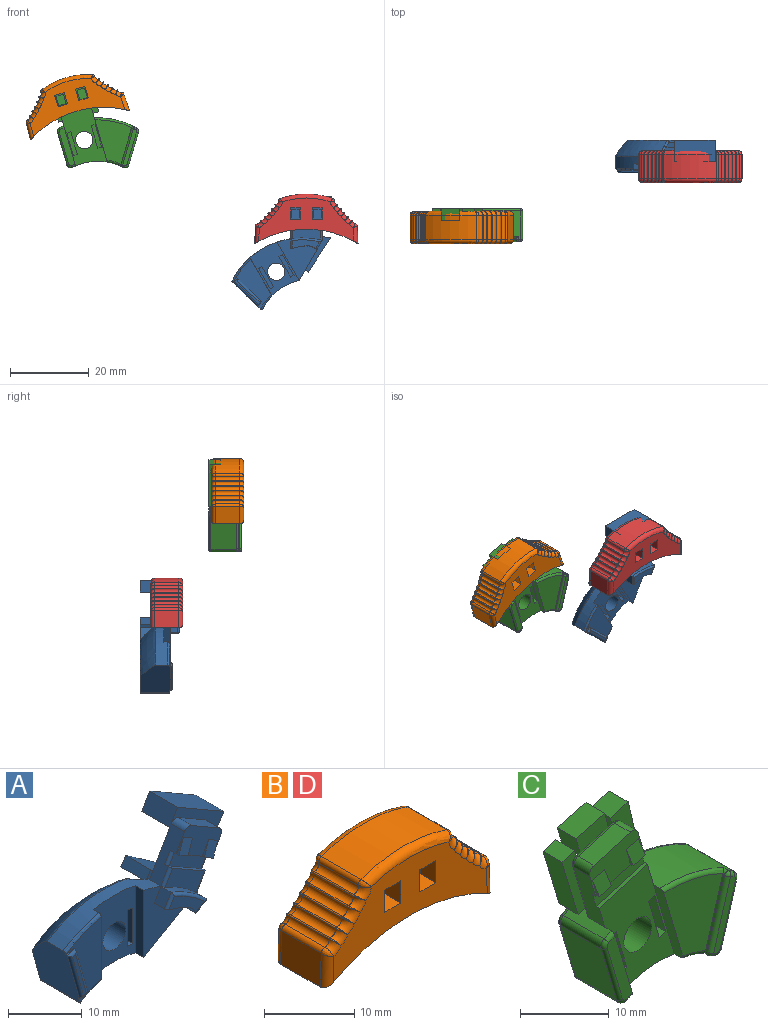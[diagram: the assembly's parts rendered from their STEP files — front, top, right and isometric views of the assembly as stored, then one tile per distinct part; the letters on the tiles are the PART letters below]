
ASSEMBLY  parts=4 mates=2
PART A: 93 faces, bbox 34.7x10.1x21.5 mm
  f0: plane 2.17x1.95mm, normal (-0.87,0,0.5), area 4.9mm2, adj f17,f19,f24,f74
  f1: plane 11.58x8mm, normal (0,-1,0), area 61.3mm2, adj f18,f23,f25,f27,f29,f40,f41,f42
  f2: plane 9.37x8mm, normal (-0.87,0,0.5), area 34.2mm2, adj f3,f8,f9,f15,f18,f53,f75,f77
  f3: plane 8.71x7.36mm, normal (0,-1,0), area 24mm2, adj f2,f4,f5,f6,f9,f10,f11,f12
  f4: plane 7.58x4.38mm, normal (0.87,0,-0.5), area 18.8mm2, adj f3,f8,f9,f15,f20,f52,f76,f78
  f5: plane 3.17x2.98mm, normal (0.08,-0.99,0.14), area 5.1mm2, adj f3,f9,f12,f14
  f6: plane 5.2x3mm, normal (0.5,0,0.87), area 15.6mm2, adj f3,f52,f53,f84
  f7: plane 7.58x6.36mm, normal (0,-1,0), area 20.1mm2, adj f15,f17,f75,f78
  f8: plane 11.14x10.83mm, normal (0,1,0), area 62mm2, adj f2,f4,f18,f81
  f9: plane 6.93x4mm, normal (-0.5,0,-0.87), area 7.3mm2, adj f2,f3,f4,f5,f10,f11,f12,f13
  f10: plane 3.17x2.98mm, normal (0.08,-0.99,0.14), area 5.1mm2, adj f3,f9,f11,f13
  f11: plane 2.17x1.25mm, normal (0.87,0,-0.5), area 0.5mm2, adj f3,f9,f10
  f12: plane 2.17x1.25mm, normal (-0.87,0,0.5), area 0.5mm2, adj f3,f5,f9
  f13: plane 2.17x1.25mm, normal (-0.87,0,0.5), area 0.5mm2, adj f3,f9,f10
  f14: plane 2.17x1.25mm, normal (0.87,0,-0.5), area 0.5mm2, adj f3,f5,f9
  f15: plane 6.93x4mm, normal (0.5,0,0.87), area 5.6mm2, adj f2,f4,f7,f16,f75,f76,f77,f78
  f16: plane 7.2x5.37mm, normal (0,-1,0), area 14.9mm2, adj f9,f15,f76,f77
  f17: cylinder r=20mm len=6.71mm, axis (0,1,0), area 12.6mm2, adj f0,f7,f18,f20,f73,f75,f78
  f18: cylinder r=20mm len=25mm, axis (0,1,0), area 50.2mm2, adj f1,f2,f8,f17,f20,f23,f24,f29
  f19: extruded ~5.8x3.46mm, area 16.6mm2, adj f0,f20,f21,f24,f72,f74
  f20: plane 10.06x6.52mm, normal (0.5,0,-0.87), area 34.4mm2, adj f4,f17,f18,f19,f23,f24,f25,f54
  f21: plane 6.88x4.81mm, normal (0,-1,0), area 10.9mm2, adj f19,f72,f73,f74
  f22: plane 6.93x5.53mm, normal (0,1,0), area 19.2mm2, adj f38,f56,f85,f89,f90
  f23: plane 11.18x1.6mm, normal (-1,0,0), area 17.9mm2, adj f1,f18,f20,f24
  f24: plane 11.18x7.89mm, normal (0,-1,0), area 46.3mm2, adj f0,f18,f19,f20,f23
  f25: cylinder r=14mm len=11.54mm, axis (0,1,0), area 70.7mm2, adj f1,f20,f26,f29,f54,f58,f60,f62
  f26: plane 8.89x1.46mm, normal (1,0,0), area 10.7mm2, adj f25,f38,f54,f63,f65,f66
  f27: cylinder r=2.2mm len=6mm, axis (0,1,0), area 82.9mm2, adj f1,f28
  f28: plane 13.39x9.12mm, normal (0,1,0), area 62.6mm2, adj f27,f30,f36,f39,f60,f62,f63,f66
  f29: plane 11.23x1.55mm, normal (1,0,0), area 16.7mm2, adj f1,f18,f25,f31,f58,f71
  f30: plane 9.75x7.81mm, normal (-0.96,0,-0.27), area 70.5mm2, adj f18,f28,f31,f32,f34,f39,f60,f70
  f31: plane 12.21x6.81mm, normal (0,-1,0), area 45.5mm2, adj f29,f30,f32,f33,f34,f58,f60,f71
  f32: plane 1.44x0.41mm, normal (0.27,0,-0.96), area 0.4mm2, adj f30,f31,f33,f68
  f33: plane 8.18x2.3mm, normal (0.96,0,0.27), area 2.1mm2, adj f31,f32,f34,f67
  f34: plane 1.44x0.41mm, normal (-0.27,0,0.96), area 0.4mm2, adj f30,f31,f33,f69
  f35: plane 7.48x2.63mm, normal (0,-1,0), area 4.6mm2, adj f67,f68,f69,f70
  f36: cylinder r=1.3mm len=5.4mm, axis (0,1,0), area 44.1mm2, adj f28,f37
  f37: plane 2.6x2.6mm, normal (0,1,0), area 5.3mm2, adj f36
  f38: cylinder r=3mm len=10.38mm, axis (0,0,-1), area 42.8mm2, adj f22,f26,f54,f57,f61,f64,f85,f86
  f39: bspline ~18.82x8.23mm, area 85.4mm2, adj f18,f28,f30,f59,f61,f64,f65
  f40: plane 6x3mm, normal (-1,0,0), area 18mm2, adj f1,f41,f44,f45
  f41: plane 3x0.42mm, normal (0,0,-1), area 1.3mm2, adj f1,f40,f42,f45
  f42: cylinder r=21.4mm len=3mm, axis (0,1,0), area 1.8mm2, adj f1,f41,f43,f45
  f43: plane 5.91x3mm, normal (1,0,0), area 17.7mm2, adj f1,f42,f44,f45
  f44: plane 3x1mm, normal (0,0,1), area 3mm2, adj f1,f40,f43,f45
  f45: plane 6x1mm, normal (0,-1,0), area 6mm2, adj f40,f41,f42,f43,f44
  f46: plane 3x0.42mm, normal (0,0,-1), area 1.3mm2, adj f1,f47,f50,f51
  f47: plane 6x3mm, normal (1,0,0), area 18mm2, adj f1,f46,f48,f51
  f48: plane 3x1mm, normal (0,0,1), area 3mm2, adj f1,f47,f49,f51
  f49: plane 5.91x3mm, normal (-1,0,0), area 17.7mm2, adj f1,f48,f50,f51
  f50: cylinder r=21.4mm len=3mm, axis (0,1,0), area 1.8mm2, adj f1,f46,f49,f51
  f51: plane 6x1mm, normal (0,-1,0), area 6mm2, adj f46,f47,f48,f49,f50
  f52: cylinder r=1mm len=2.6mm, axis (0,1,0), area 4.1mm2, adj f3,f4,f6,f84
  f53: cylinder r=1mm len=2.6mm, axis (0,1,0), area 4.1mm2, adj f2,f3,f6,f84
  f54: bspline ~4.68x3.45mm, area 3mm2, adj f20,f25,f26,f38,f55,f86,f87
  f55: cylinder r=0.45mm len=7.06mm, axis (0.87,0,0.5), area 5.4mm2, adj f20,f54,f56,f87
  f56: torus R=19.55mm, axis (0,-1,0), area 5.6mm2, adj f18,f22,f55,f57,f87
  f57: bspline ~3.69x1.67mm, area 1.9mm2, adj f18,f38,f56,f59
  f58: torus R=14.45mm, axis (0,-1,0), area 3mm2, adj f25,f29,f31,f60
  f59: bspline ~0.44x0.28mm, area 0mm2, adj f39,f57,f61
  f60: cylinder r=0.45mm len=7.5mm, axis (0,1,0), area 6.1mm2, adj f25,f28,f30,f31,f58,f62
  f61: bspline ~2.6x2.46mm, area 1.6mm2, adj f38,f39,f59,f64
  f62: torus R=14.45mm, axis (0,-1,0), area 8.5mm2, adj f25,f28,f60,f63
  f63: cylinder r=0.45mm len=7.03mm, axis (0,0,1), area 4.8mm2, adj f26,f28,f62,f66
  f64: bspline ~0.42x0.4mm, area 0.1mm2, adj f38,f39,f61,f65
  f65: bspline ~1.97x1.8mm, area 1.5mm2, adj f26,f39,f64,f66
  f66: bspline ~0.45x0.45mm, area 0.1mm2, adj f26,f28,f63,f65
  f67: cylinder r=0.45mm len=8.31mm, axis (0.27,0,-0.96), area 5.7mm2, adj f33,f35,f68,f69
  f68: cylinder r=0.45mm len=1.57mm, axis (-0.96,0,-0.27), area 0.7mm2, adj f32,f35,f67,f70
  f69: cylinder r=0.45mm len=1.57mm, axis (0.96,0,0.27), area 0.7mm2, adj f34,f35,f67,f70
  f70: cylinder r=0.45mm len=8.31mm, axis (-0.27,0,0.96), area 5.7mm2, adj f30,f35,f68,f69
  f71: torus R=19.55mm, axis (0,-1,0), area 5.3mm2, adj f18,f29,f30,f31
  f72: cylinder r=0.45mm len=2.46mm, axis (-0.87,0,-0.5), area 1.6mm2, adj f19,f20,f21,f73
  f73: torus R=19.55mm, axis (0,-1,0), area 5.3mm2, adj f17,f21,f72,f74
  f74: cylinder r=0.45mm len=2.39mm, axis (0.5,0,0.87), area 1.6mm2, adj f0,f19,f21,f73
  f75: cylinder r=0.45mm len=2.75mm, axis (0.5,0,0.87), area 2mm2, adj f2,f7,f15,f17
  f76: cylinder r=0.45mm len=2.04mm, axis (-0.5,0,-0.87), area 1.5mm2, adj f4,f9,f15,f16
  f77: cylinder r=0.45mm len=2.04mm, axis (0.5,0,0.87), area 1.5mm2, adj f2,f9,f15,f16
  f78: cylinder r=0.45mm len=3.13mm, axis (-0.5,0,-0.87), area 2.3mm2, adj f4,f7,f15,f17
  f79: plane 10.4x7.74mm, normal (0,1,0), area 30.8mm2, adj f2,f80,f81,f82,f83
  f80: plane 5.4x1.86mm, normal (-0.52,0,-0.85), area 11.8mm2, adj f79,f81,f83,f84
  f81: plane 6.93x5.4mm, normal (-0.5,0,-0.87), area 43.2mm2, adj f2,f8,f79,f80
  f82: plane 8.9x5.4mm, normal (0.5,0,0.87), area 55.5mm2, adj f2,f79,f83,f84
  f83: plane 5.4x2.6mm, normal (0.85,0,-0.53), area 16.5mm2, adj f79,f80,f82,f84
  f84: plane 10.15x7.74mm, normal (0,-1,0), area 19.2mm2, adj f2,f4,f6,f52,f53,f80,f82,f83
  f85: plane 5.84x4.8mm, normal (-0.48,0,0.88), area 32mm2, adj f22,f38,f86,f88,f89
  f86: plane 4.8x2.15mm, normal (-0.99,0,-0.13), area 10.4mm2, adj f38,f54,f85,f87,f88,f92
  f87: plane 10.51x9.6mm, normal (0,-1,0), area 26.2mm2, adj f54,f55,f56,f86,f90,f91,f92
  f88: plane 10.51x9.7mm, normal (0,1,0), area 33mm2, adj f85,f86,f89,f90,f91,f92
  f89: plane 5.3x4.8mm, normal (-0.57,0,-0.82), area 31.1mm2, adj f22,f85,f88,f90
  f90: plane 4.8x1.42mm, normal (-0.82,0,0.57), area 8.3mm2, adj f22,f87,f88,f89,f91
  f91: plane 8.16x5.73mm, normal (0.57,0,0.82), area 47.9mm2, adj f87,f88,f90,f92
  f92: plane 9.4x4.8mm, normal (0.45,0,-0.89), area 50.6mm2, adj f86,f87,f88,f91
PART B: 107 faces, bbox 26.2x8.2x14.3 mm
  f0: plane 8.3x1.05mm, normal (0,1,0), area 6.8mm2, adj f1,f5,f21,f33
  f1: plane 7.2x3.3mm, normal (-1,0,0), area 23.2mm2, adj f0,f3,f5,f22,f23,f32,f33,f34
  f2: plane 24.15x11.01mm, normal (0,-1,0), area 137mm2, adj f5,f24,f25,f26,f27,f28,f29,f30
  f3: plane 8.3x4.75mm, normal (0,1,0), area 24.5mm2, adj f1,f21,f22,f24,f25,f26,f27,f28
  f4: plane 6.2x4.47mm, normal (-1,0,0.04), area 27.7mm2, adj f5,f48,f49,f78
  f5: cylinder r=25mm len=26.2mm, axis (0,1,0), area 197.6mm2, adj f0,f1,f2,f4,f6,f20,f21,f23
  f6: plane 6.2x4.47mm, normal (1,0,0.04), area 27.7mm2, adj f5,f45,f77,f106
  f7: cylinder r=0.68mm len=6.2mm, axis (0,1,0), area 7.3mm2, adj f35,f45,f75,f104
  f8: cylinder r=0.68mm len=6.2mm, axis (0,1,0), area 9.1mm2, adj f35,f36,f73,f102
  f9: cylinder r=0.68mm len=6.2mm, axis (0,1,0), area 9.1mm2, adj f36,f37,f71,f100
  f10: cylinder r=0.68mm len=6.2mm, axis (0,1,0), area 9.1mm2, adj f37,f38,f69,f98
  f11: cylinder r=0.68mm len=6.2mm, axis (0,1,0), area 9.1mm2, adj f38,f39,f67,f96
  f12: cylinder r=0.68mm len=6.2mm, axis (0,1,0), area 7.9mm2, adj f39,f46,f65,f94
  f13: cylinder r=20mm len=13.45mm, axis (0,1,0), area 85mm2, adj f46,f47,f63,f92
  f14: cylinder r=0.68mm len=6.2mm, axis (0,1,0), area 7.9mm2, adj f40,f47,f61,f90
  f15: cylinder r=0.68mm len=6.2mm, axis (0,1,0), area 9.1mm2, adj f40,f41,f59,f88
  f16: cylinder r=0.68mm len=6.2mm, axis (0,1,0), area 9.1mm2, adj f41,f42,f57,f86
  f17: cylinder r=0.68mm len=6.2mm, axis (0,1,0), area 9.1mm2, adj f42,f43,f55,f84
  f18: cylinder r=0.68mm len=6.2mm, axis (0,1,0), area 9.1mm2, adj f43,f44,f53,f82
  f19: cylinder r=0.68mm len=6.2mm, axis (0,1,0), area 7.3mm2, adj f44,f48,f51,f80
  f20: plane 24.15x11.01mm, normal (0,1,0), area 152mm2, adj f5,f78,f80,f82,f84,f86,f88,f90
  f21: plane 7.2x3.3mm, normal (1,0,0), area 23.2mm2, adj f0,f3,f5,f22,f23,f32,f33,f34
  f22: plane 8.3x3.3mm, normal (0,0,-1), area 27.4mm2, adj f1,f3,f21,f23
  f23: plane 8.3x7.2mm, normal (0,-1,0), area 57.8mm2, adj f1,f5,f21,f22
  f24: plane 3x2.45mm, normal (1,0,0), area 7.4mm2, adj f2,f3,f25,f26
  f25: plane 2.5x2.45mm, normal (0,0,1), area 6.1mm2, adj f2,f3,f24,f27
  f26: plane 2.5x2.45mm, normal (0,0,-1), area 6.1mm2, adj f2,f3,f24,f27
  f27: plane 3x2.45mm, normal (-1,0,0), area 7.4mm2, adj f2,f3,f25,f26
  f28: plane 3x2.45mm, normal (1,0,0), area 7.4mm2, adj f2,f3,f29,f30
  f29: plane 2.5x2.45mm, normal (0,0,1), area 6.1mm2, adj f2,f3,f28,f31
  f30: plane 2.5x2.45mm, normal (0,0,-1), area 6.1mm2, adj f2,f3,f28,f31
  f31: plane 3x2.45mm, normal (-1,0,0), area 7.4mm2, adj f2,f3,f29,f30
  f32: plane 8.3x0.4mm, normal (0,0,1), area 3.3mm2, adj f1,f3,f21,f34
  f33: plane 8.3x0.4mm, normal (0,0,-1), area 3.3mm2, adj f0,f1,f21,f34
  f34: plane 8.3x1.4mm, normal (0,1,0), area 11.6mm2, adj f1,f21,f32,f33
  f35: cylinder r=0.1mm len=6.2mm, axis (0,1,0), area 1.3mm2, adj f7,f8,f74,f103
  f36: cylinder r=0.1mm len=6.2mm, axis (0,1,0), area 1.3mm2, adj f8,f9,f72,f101
  f37: cylinder r=0.1mm len=6.2mm, axis (0,1,0), area 1.3mm2, adj f9,f10,f70,f99
  f38: cylinder r=0.1mm len=6.2mm, axis (0,1,0), area 1.3mm2, adj f10,f11,f68,f97
  f39: cylinder r=0.1mm len=6.2mm, axis (0,1,0), area 1.3mm2, adj f11,f12,f66,f95
  f40: cylinder r=0.1mm len=6.2mm, axis (0,1,0), area 1.3mm2, adj f14,f15,f60,f89
  f41: cylinder r=0.1mm len=6.2mm, axis (0,1,0), area 1.3mm2, adj f15,f16,f58,f87
  f42: cylinder r=0.1mm len=6.2mm, axis (0,1,0), area 1.3mm2, adj f16,f17,f56,f85
  f43: cylinder r=0.1mm len=6.2mm, axis (0,1,0), area 1.3mm2, adj f17,f18,f54,f83
  f44: cylinder r=0.1mm len=6.2mm, axis (0,1,0), area 1.3mm2, adj f18,f19,f52,f81
  f45: cylinder r=0.6mm len=6.2mm, axis (0,1,0), area 5.6mm2, adj f6,f7,f76,f105
  f46: cylinder r=0.6mm len=6.2mm, axis (0,-1,0), area 5.3mm2, adj f12,f13,f64,f93
  f47: cylinder r=0.6mm len=6.2mm, axis (0,-1,0), area 5.3mm2, adj f13,f14,f62,f91
  f48: cylinder r=0.6mm len=6.2mm, axis (0,1,0), area 5.6mm2, adj f4,f19,f50,f79
  f49: cylinder r=1mm len=4.51mm, axis (0.04,0,1), area 6.5mm2, adj f2,f4,f5,f50
  f50: bspline ~1x0.99mm, area 0.9mm2, adj f48,f49,f51
  f51: torus R=1.68mm, axis (0,-1,0), area 2mm2, adj f2,f19,f50,f52
  f52: bspline ~1.04x1.03mm, area 0.1mm2, adj f44,f51,f53
  f53: torus R=1.68mm, axis (0,-1,0), area 2.3mm2, adj f2,f18,f52,f54
  f54: bspline ~1.04x0.98mm, area 0.1mm2, adj f43,f53,f55
  f55: torus R=1.68mm, axis (0,-1,0), area 2.3mm2, adj f2,f17,f54,f56
  f56: bspline ~1.04x0.99mm, area 0.1mm2, adj f42,f55,f57
  f57: torus R=1.68mm, axis (0,-1,0), area 2.3mm2, adj f2,f16,f56,f58
  f58: bspline ~1.04x1.04mm, area 0.1mm2, adj f41,f57,f59
  f59: torus R=1.68mm, axis (0,-1,0), area 2.3mm2, adj f2,f15,f58,f60
  f60: bspline ~1.08x1.04mm, area 0.1mm2, adj f40,f59,f61
  f61: torus R=1.68mm, axis (0,-1,0), area 2.3mm2, adj f2,f14,f60,f62
  f62: bspline ~1.26x1.11mm, area 0.8mm2, adj f47,f61,f63
  f63: torus R=19mm, axis (0,-1,0), area 20.8mm2, adj f2,f13,f62,f64
  f64: bspline ~1.26x1.11mm, area 0.8mm2, adj f46,f63,f65
  f65: torus R=1.68mm, axis (0,-1,0), area 2.3mm2, adj f2,f12,f64,f66
  f66: bspline ~1.08x1.04mm, area 0.1mm2, adj f39,f65,f67
  f67: torus R=1.68mm, axis (0,-1,0), area 2.3mm2, adj f2,f11,f66,f68
  f68: bspline ~1.04x1.04mm, area 0.1mm2, adj f38,f67,f69
  f69: torus R=1.68mm, axis (0,-1,0), area 2.3mm2, adj f2,f10,f68,f70
  f70: bspline ~1.04x0.99mm, area 0.1mm2, adj f37,f69,f71
  f71: torus R=1.68mm, axis (0,-1,0), area 2.3mm2, adj f2,f9,f70,f72
  f72: bspline ~1.04x0.98mm, area 0.1mm2, adj f36,f71,f73
  f73: torus R=1.68mm, axis (0,-1,0), area 2.3mm2, adj f2,f8,f72,f74
  f74: bspline ~1.04x1.03mm, area 0.1mm2, adj f35,f73,f75
  f75: torus R=1.68mm, axis (0,-1,0), area 2mm2, adj f2,f7,f74,f76
  f76: bspline ~1.27x0.99mm, area 0.9mm2, adj f45,f75,f77
  f77: cylinder r=1mm len=4.51mm, axis (0.04,0,-1), area 6.5mm2, adj f2,f5,f6,f76
  f78: cylinder r=1mm len=4.51mm, axis (-0.04,0,-1), area 6.5mm2, adj f4,f5,f20,f79
  f79: bspline ~1.27x0.99mm, area 0.9mm2, adj f48,f78,f80
  f80: torus R=1.68mm, axis (0,-1,0), area 2mm2, adj f19,f20,f79,f81
  f81: bspline ~1.16x1.03mm, area 0.1mm2, adj f44,f80,f82
  f82: torus R=1.68mm, axis (0,-1,0), area 2.3mm2, adj f18,f20,f81,f83
  f83: bspline ~1.16x0.98mm, area 0.1mm2, adj f43,f82,f84
  f84: torus R=1.68mm, axis (0,-1,0), area 2.3mm2, adj f17,f20,f83,f85
  f85: bspline ~1.16x0.99mm, area 0.1mm2, adj f42,f84,f86
  f86: torus R=1.68mm, axis (0,-1,0), area 2.3mm2, adj f16,f20,f85,f87
  f87: bspline ~1.16x1.04mm, area 0.1mm2, adj f41,f86,f88
  f88: torus R=1.68mm, axis (0,-1,0), area 2.3mm2, adj f15,f20,f87,f89
  f89: bspline ~1.16x1.08mm, area 0.1mm2, adj f40,f88,f90
  f90: torus R=1.68mm, axis (0,-1,0), area 2.3mm2, adj f14,f20,f89,f91
  f91: bspline ~1.26x1.11mm, area 0.8mm2, adj f47,f90,f92
  f92: torus R=19mm, axis (0,-1,0), area 20.8mm2, adj f13,f20,f91,f93
  f93: bspline ~1.26x1.11mm, area 0.8mm2, adj f46,f92,f94
  f94: torus R=1.68mm, axis (0,-1,0), area 2.3mm2, adj f12,f20,f93,f95
  f95: bspline ~1.16x1.08mm, area 0.1mm2, adj f39,f94,f96
  f96: torus R=1.68mm, axis (0,-1,0), area 2.3mm2, adj f11,f20,f95,f97
  f97: bspline ~1.16x1.04mm, area 0.1mm2, adj f38,f96,f98
  f98: torus R=1.68mm, axis (0,-1,0), area 2.3mm2, adj f10,f20,f97,f99
  f99: bspline ~1.16x0.99mm, area 0.1mm2, adj f37,f98,f100
  f100: torus R=1.68mm, axis (0,-1,0), area 2.3mm2, adj f9,f20,f99,f101
  f101: bspline ~1.16x0.98mm, area 0.1mm2, adj f36,f100,f102
  f102: torus R=1.68mm, axis (0,-1,0), area 2.3mm2, adj f8,f20,f101,f103
  f103: bspline ~1.16x1.03mm, area 0.1mm2, adj f35,f102,f104
  f104: torus R=1.68mm, axis (0,-1,0), area 2mm2, adj f7,f20,f103,f105
  f105: bspline ~1x0.99mm, area 0.9mm2, adj f45,f104,f106
  f106: cylinder r=1mm len=4.51mm, axis (-0.04,0,1), area 6.5mm2, adj f5,f6,f20,f105
PART C: 93 faces, bbox 23.2x8.4x23.5 mm
  f0: plane 10.38x8.77mm, normal (0,1,0), area 52.5mm2, adj f7,f53,f55,f57,f78,f79,f83,f84
  f1: plane 2.96x2.62mm, normal (-0.04,-0.99,0.15), area 5.1mm2, adj f2,f3,f36,f38
  f2: plane 1.92x0.57mm, normal (0.28,0.02,-0.96), area 0.8mm2, adj f1,f31,f36,f38
  f3: plane 8.65x6.14mm, normal (0,-1,0), area 24mm2, adj f1,f4,f5,f19,f31,f33,f35,f36
  f4: plane 8.43x2.5mm, normal (0.96,0,0.28), area 21mm2, adj f3,f6,f7,f30,f31,f32,f39,f53
  f5: plane 8.14x2.5mm, normal (-0.96,0,-0.28), area 20.2mm2, adj f3,f6,f7,f30,f31,f32,f40,f57
  f6: plane 15.53x11.94mm, normal (0,-1,0), area 84.8mm2, adj f4,f5,f8,f13,f15,f16,f20,f21
  f7: cylinder r=20mm len=19.62mm, axis (0,1,0), area 101.8mm2, adj f0,f4,f5,f13,f16,f41,f44,f52
  f8: cylinder r=14mm len=12.88mm, axis (0,1,0), area 79.1mm2, adj f6,f13,f16,f42,f43,f45,f62,f65
  f9: plane 8.24x7.3mm, normal (0.96,0,-0.28), area 62.7mm2, adj f43,f44,f48,f64
  f10: plane 9.23x2.72mm, normal (-0.96,0,0.28), area 2.9mm2, adj f14,f59,f62,f65,f66
  f11: plane 9.47x3.52mm, normal (0,-1,0), area 9.5mm2, adj f60,f61,f64,f66,f67,f69
  f12: plane 19.64x11.68mm, normal (0,1,0), area 159.8mm2, adj f15,f45,f46,f47,f48,f49,f50,f51
  f13: plane 11.23x3.34mm, normal (-0.96,0,-0.28), area 17.4mm2, adj f6,f7,f8,f14,f58,f62
  f14: plane 11.23x9.37mm, normal (0,-1,0), area 66.4mm2, adj f10,f13,f58,f59,f62
  f15: cylinder r=2.2mm len=6mm, axis (0,1,0), area 82.9mm2, adj f6,f12
  f16: plane 10.26x3.04mm, normal (0.96,0,0.28), area 15.9mm2, adj f6,f7,f8,f18,f70,f74
  f17: plane 8.24x6.5mm, normal (-0.96,0,-0.28), area 55.8mm2, adj f41,f42,f49,f72
  f18: plane 9.7x3.98mm, normal (0,-1,0), area 14.3mm2, adj f16,f70,f71,f72,f73,f74
  f19: plane 5.76x2.5mm, normal (-0.28,0,0.96), area 15mm2, adj f3,f39,f40,f55
  f20: plane 3x1.01mm, normal (-0.28,0,0.96), area 3.1mm2, adj f6,f21,f23,f24
  f21: plane 5.76x3mm, normal (-0.96,0,-0.28), area 18mm2, adj f6,f20,f22,f24
  f22: plane 3x1.01mm, normal (0.28,0,-0.96), area 3.2mm2, adj f6,f21,f23,f24
  f23: plane 5.76x3mm, normal (0.96,0,0.28), area 18mm2, adj f6,f20,f22,f24
  f24: plane 6.05x2.7mm, normal (0,-1,0), area 6.3mm2, adj f20,f21,f22,f23
  f25: plane 5.76x3mm, normal (0.96,0,0.28), area 18mm2, adj f6,f26,f28,f29
  f26: plane 3x1.01mm, normal (-0.28,0,0.96), area 3.1mm2, adj f6,f25,f27,f29
  f27: plane 5.76x3mm, normal (-0.96,0,-0.28), area 18mm2, adj f6,f26,f28,f29
  f28: plane 3x1.01mm, normal (0.28,0,-0.96), area 3.1mm2, adj f6,f25,f27,f29
  f29: plane 6.05x2.7mm, normal (0,-1,0), area 6.3mm2, adj f25,f26,f27,f28
  f30: plane 7.68x2.26mm, normal (-0.28,0,0.96), area 4mm2, adj f4,f5,f6,f32
  f31: plane 7.68x2.26mm, normal (0.28,0,-0.96), area 4mm2, adj f2,f3,f4,f5,f32,f34
  f32: plane 8.24x4.18mm, normal (0,-1,0), area 16mm2, adj f4,f5,f30,f31
  f33: plane 2.96x2.62mm, normal (-0.04,-0.99,0.15), area 5.1mm2, adj f3,f34,f35,f37
  f34: plane 1.92x0.57mm, normal (0.28,0.02,-0.96), area 0.8mm2, adj f31,f33,f35,f37
  f35: plane 2.4x0.71mm, normal (0.96,0,0.28), area 0.5mm2, adj f3,f33,f34
  f36: plane 2.4x0.71mm, normal (-0.96,0,-0.28), area 0.5mm2, adj f1,f2,f3
  f37: plane 2.4x0.71mm, normal (-0.96,0,-0.28), area 0.5mm2, adj f3,f33,f34
  f38: plane 2.4x0.71mm, normal (0.96,0,0.28), area 0.5mm2, adj f1,f2,f3
  f39: cylinder r=1mm len=2.5mm, axis (0,1,0), area 3.9mm2, adj f3,f4,f19,f54
  f40: cylinder r=1mm len=2.5mm, axis (0,1,0), area 3.9mm2, adj f3,f5,f19,f56
  f41: cylinder r=1mm len=6.5mm, axis (0,1,0), area 8.7mm2, adj f7,f17,f51,f71
  f42: cylinder r=1mm len=6.5mm, axis (0,1,0), area 11.5mm2, adj f8,f17,f47,f73
  f43: cylinder r=1mm len=7.3mm, axis (0,1,0), area 12.9mm2, adj f8,f9,f46,f67
  f44: cylinder r=1mm len=7.3mm, axis (0,1,0), area 9.8mm2, adj f7,f9,f50,f61
  f45: torus R=14.5mm, axis (0,-1,0), area 10.6mm2, adj f8,f12,f46,f47
  f46: torus R=0.5mm, axis (0,-1,0), area 1.1mm2, adj f12,f43,f45,f48
  f47: torus R=0.5mm, axis (0,-1,0), area 1.1mm2, adj f12,f42,f45,f49
  f48: cylinder r=0.5mm len=8.38mm, axis (0.28,0,0.96), area 6.7mm2, adj f9,f12,f46,f50
  f49: cylinder r=0.5mm len=8.38mm, axis (0.28,0,-0.96), area 6.7mm2, adj f12,f17,f47,f51
  f50: torus R=0.5mm, axis (0,-1,0), area 0.9mm2, adj f12,f44,f48,f52
  f51: torus R=0.5mm, axis (0,-1,0), area 0.9mm2, adj f12,f41,f49,f52
  f52: torus R=19.5mm, axis (0,-1,0), area 16mm2, adj f7,f12,f50,f51
  f53: cylinder r=0.5mm len=8.57mm, axis (-0.28,0,0.96), area 6.9mm2, adj f0,f4,f7,f54,f81
  f54: torus R=0.5mm, axis (0,-1,0), area 1mm2, adj f39,f53,f55,f81
  f55: cylinder r=0.5mm len=5.9mm, axis (-0.96,0,-0.28), area 4.7mm2, adj f0,f19,f54,f56,f75,f81,f87
  f56: torus R=0.5mm, axis (0,-1,0), area 1mm2, adj f40,f55,f57,f75
  f57: cylinder r=0.5mm len=8.28mm, axis (0.28,0,-0.96), area 6.6mm2, adj f0,f5,f7,f56,f75
  f58: torus R=19.5mm, axis (0,-1,0), area 8mm2, adj f7,f13,f14,f59
  f59: cylinder r=0.5mm len=0.8mm, axis (0,1,0), area 0.4mm2, adj f7,f10,f14,f58,f63
  f60: torus R=19.5mm, axis (0,-1,0), area 0.5mm2, adj f7,f11,f61,f63
  f61: torus R=0.5mm, axis (0,-1,0), area 0.9mm2, adj f11,f44,f60,f64
  f62: torus R=14.5mm, axis (0,-1,0), area 3mm2, adj f8,f10,f13,f14,f65
  f63: sphere r=0.5mm, area 0.5mm2, adj f59,f60,f66
  f64: cylinder r=0.5mm len=8.38mm, axis (-0.28,0,-0.96), area 6.7mm2, adj f9,f11,f61,f67
  f65: cylinder r=0.5mm len=0.8mm, axis (0,1,0), area 0.4mm2, adj f8,f10,f62,f68
  f66: cylinder r=0.5mm len=9.37mm, axis (0.28,0,0.96), area 7.6mm2, adj f10,f11,f63,f68
  f67: torus R=0.5mm, axis (0,-1,0), area 1.1mm2, adj f11,f43,f64,f69
  f68: sphere r=0.5mm, area 0.3mm2, adj f65,f66,f69
  f69: torus R=14.5mm, axis (0,-1,0), area 0.3mm2, adj f8,f11,f67,f68
  f70: torus R=19.5mm, axis (0,-1,0), area 0.9mm2, adj f7,f16,f18,f71
  f71: torus R=0.5mm, axis (0,-1,0), area 0.9mm2, adj f18,f41,f70,f72
  f72: cylinder r=0.5mm len=8.38mm, axis (-0.28,0,0.96), area 6.7mm2, adj f17,f18,f71,f73
  f73: torus R=0.5mm, axis (0,-1,0), area 1.1mm2, adj f18,f42,f72,f74
  f74: torus R=14.5mm, axis (0,-1,0), area 0.7mm2, adj f8,f16,f18,f73
  f75: plane 9.08x3.97mm, normal (0,-1,0), area 14mm2, adj f55,f56,f57,f77,f78,f79,f80
  f76: plane 9.08x4.3mm, normal (0,1,0), area 17.4mm2, adj f77,f78,f79,f80
  f77: plane 3x2.03mm, normal (-0.28,0,0.96), area 6.3mm2, adj f75,f76,f78,f80
  f78: plane 8.56x3mm, normal (0.97,0,0.26), area 26.6mm2, adj f0,f75,f76,f77,f79
  f79: plane 3x1.73mm, normal (0.29,0,-0.96), area 5.4mm2, adj f0,f75,f76,f78,f80
  f80: plane 8.5x3mm, normal (-0.96,0,-0.29), area 26.6mm2, adj f75,f76,f77,f79
  f81: plane 9.24x5.01mm, normal (0,-1,0), area 20.7mm2, adj f53,f54,f55,f83,f84,f85,f86
  f82: plane 9.31x5.01mm, normal (0,1,0), area 24.4mm2, adj f83,f84,f85,f86
  f83: plane 3x2.42mm, normal (0.16,0,-0.99), area 7.4mm2, adj f0,f81,f82,f84,f86
  f84: plane 8.49x3mm, normal (-0.96,0,-0.29), area 26.6mm2, adj f0,f81,f82,f83,f85
  f85: plane 3x2.85mm, normal (-0.28,0,0.96), area 8.9mm2, adj f81,f82,f84,f86
  f86: plane 8.92x3mm, normal (0.97,0,0.24), area 27.5mm2, adj f81,f82,f83,f85
  f87: plane 5.14x3.58mm, normal (0,-1,0), area 11.4mm2, adj f55,f89,f91,f92
  f88: plane 5.25x4.01mm, normal (0,1,0), area 13.4mm2, adj f89,f90,f91,f92
  f89: plane 3x2.72mm, normal (0.97,0,0.24), area 8.4mm2, adj f0,f87,f88,f90,f91
  f90: plane 4.41x3mm, normal (0.28,0,-0.96), area 13.8mm2, adj f0,f88,f89,f92
  f91: plane 4.59x3mm, normal (-0.25,0,0.97), area 14.2mm2, adj f87,f88,f89,f92
  f92: plane 3x2.84mm, normal (-0.96,0,-0.28), area 8.9mm2, adj f0,f87,f88,f90,f91
PART D: same geometry as B
PLACE A rot(axis=(0,-1,0),30deg) t=(24.01,19.89,-22.91)mm fixed
PLACE B rot(axis=(0,-1,0),16.4deg) t=(-28.91,1.8,21.43)mm
PLACE C t=(-23.3,2.45,8.77)mm fixed
PLACE D t=(29.57,17.29,-8.46)mm
MATE fastened A.f6 <-> D.f22  axis (0,0,1) through (29.57,13.19,-1.6)mm
MATE fastened C.f19 <-> B.f22  axis (-0.28,0,0.96) through (-30.85,-2.3,28)mm
